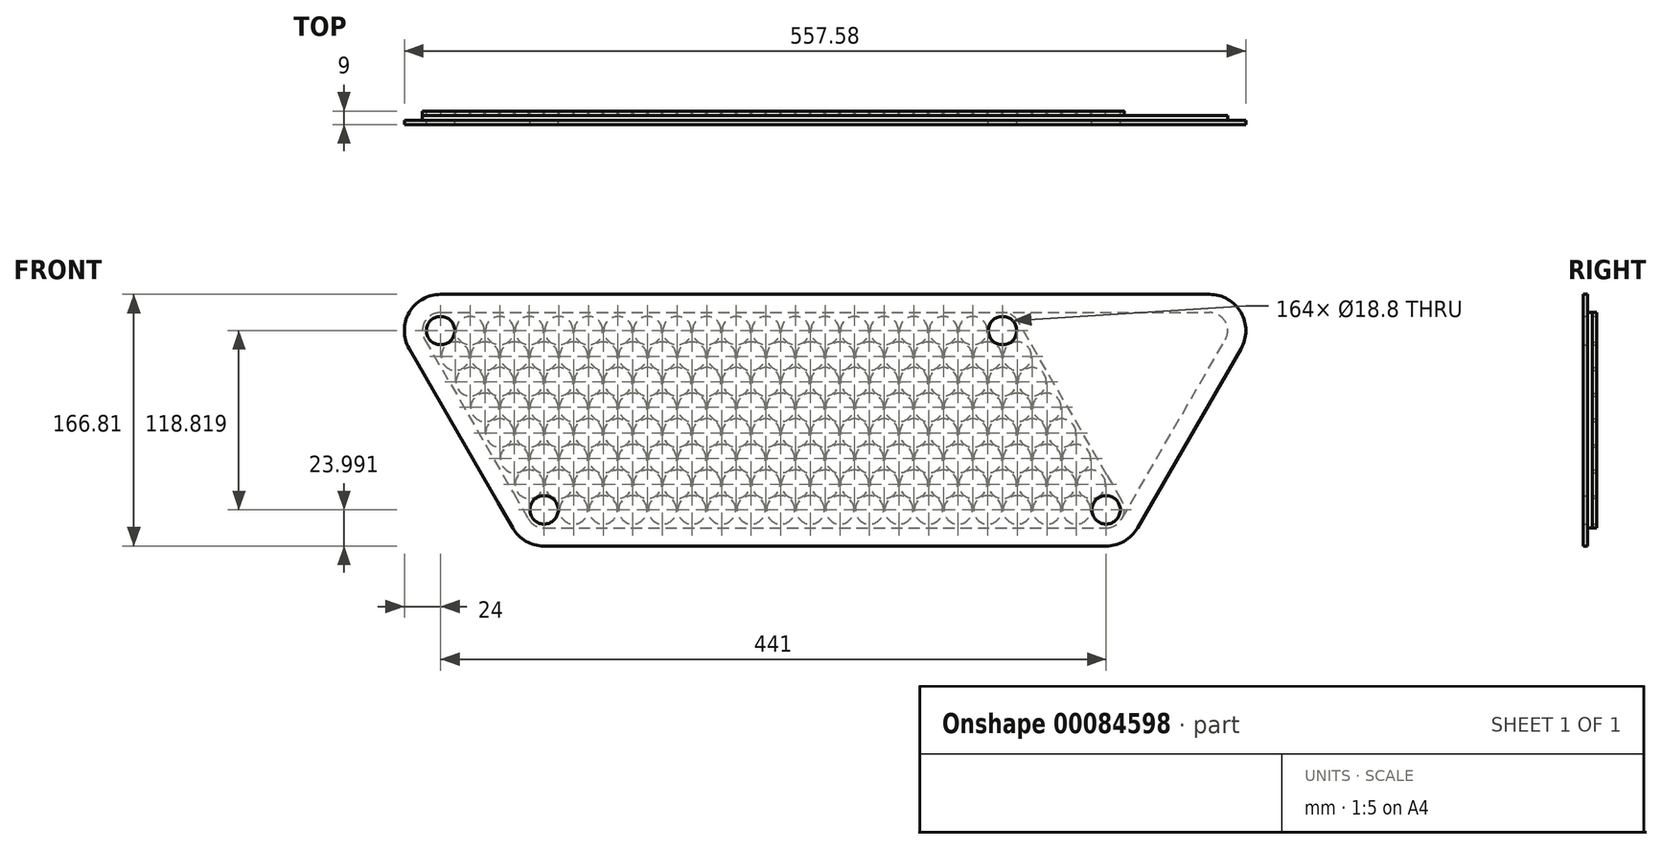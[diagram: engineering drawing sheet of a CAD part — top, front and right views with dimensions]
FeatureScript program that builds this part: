
annotation { "Feature Type Name" : "Feature", "Feature Type Description" : "" }
export const myFeature = defineFeature(function(context is Context, id is Id, definition is map)
    precondition{}
    {
        {
            var Q0;
            Q0=qCreatedBy(makeId("Front.planeOp"),FACE);
            var sketch = newSketch(context, id + "F0", { "sketchPlane" : qUnion([Q0]) });
            skLineSegment(sketch, "E0", {"start": v(0, 0) * mm, "end": v(79.44, 0) * mm, "construction": true});
            skLineSegment(sketch, "E1", {"start": v(0, 0) * mm, "end": v(43.4, -75.16) * mm, "construction": true});
            skCircle(sketch, "E2", {"center": v(0, 0) * mm, "radius": 9.4 * mm});
            skCircle(sketch, "E3.1.0.0", {"center": v(19.6, 0) * mm, "radius": 9.4 * mm});
            skCircle(sketch, "E3.2.0.0", {"center": v(39.2, 0) * mm, "radius": 9.4 * mm});
            skCircle(sketch, "E3.3.0.0", {"center": v(58.8, 0) * mm, "radius": 9.4 * mm});
            skCircle(sketch, "E3.4.0.0", {"center": v(78.4, 0) * mm, "radius": 9.4 * mm});
            skCircle(sketch, "E3.5.0.0", {"center": v(98, 0) * mm, "radius": 9.4 * mm});
            skCircle(sketch, "E3.6.0.0", {"center": v(117.6, 0) * mm, "radius": 9.4 * mm});
            skCircle(sketch, "E3.7.0.0", {"center": v(137.2, 0) * mm, "radius": 9.4 * mm});
            skCircle(sketch, "E3.8.0.0", {"center": v(156.8, 0) * mm, "radius": 9.4 * mm});
            skCircle(sketch, "E3.9.0.0", {"center": v(176.4, 0) * mm, "radius": 9.4 * mm});
            skCircle(sketch, "E3.10.0.0", {"center": v(196, 0) * mm, "radius": 9.4 * mm});
            skCircle(sketch, "E3.11.0.0", {"center": v(215.6, 0) * mm, "radius": 9.4 * mm});
            skCircle(sketch, "E3.12.0.0", {"center": v(235.2, 0) * mm, "radius": 9.4 * mm});
            skCircle(sketch, "E3.13.0.0", {"center": v(254.8, 0) * mm, "radius": 9.4 * mm});
            skCircle(sketch, "E3.14.0.0", {"center": v(274.4, 0) * mm, "radius": 9.4 * mm});
            skCircle(sketch, "E3.15.0.0", {"center": v(294, 0) * mm, "radius": 9.4 * mm});
            skCircle(sketch, "E3.16.0.0", {"center": v(313.6, 0) * mm, "radius": 9.4 * mm});
            skCircle(sketch, "E3.17.0.0", {"center": v(333.2, 0) * mm, "radius": 9.4 * mm});
            skCircle(sketch, "E3.18.0.0", {"center": v(352.8, 0) * mm, "radius": 9.4 * mm});
            skCircle(sketch, "E3.19.0.0", {"center": v(372.4, 0) * mm, "radius": 9.4 * mm});
            skLineSegment(sketch, "E3.direction1", {"start": v(0, 0) * mm, "end": v(19.6, 0) * mm, "construction": true});
            skCircle(sketch, "E4.1.0.0", {"center": v(9.8, -16.97) * mm, "radius": 9.4 * mm});
            skCircle(sketch, "E4.2.0.0", {"center": v(19.6, -33.95) * mm, "radius": 9.4 * mm});
            skCircle(sketch, "E4.3.0.0", {"center": v(29.4, -50.92) * mm, "radius": 9.4 * mm});
            skCircle(sketch, "E4.4.0.0", {"center": v(39.2, -67.9) * mm, "radius": 9.4 * mm});
            skCircle(sketch, "E4.5.0.0", {"center": v(49, -84.87) * mm, "radius": 9.4 * mm});
            skCircle(sketch, "E4.6.0.0", {"center": v(58.8, -101.84) * mm, "radius": 9.4 * mm});
            skLineSegment(sketch, "E4.direction1", {"start": v(0, 0) * mm, "end": v(9.8, -16.97) * mm, "construction": true});
            skCircle(sketch, "E5.1.0.0", {"center": v(29.4, -16.97) * mm, "radius": 9.4 * mm});
            skCircle(sketch, "E5.1.0.1", {"center": v(39.2, -33.95) * mm, "radius": 9.4 * mm});
            skCircle(sketch, "E5.1.0.2", {"center": v(49, -50.92) * mm, "radius": 9.4 * mm});
            skCircle(sketch, "E5.1.0.3", {"center": v(58.8, -67.9) * mm, "radius": 9.4 * mm});
            skCircle(sketch, "E5.1.0.4", {"center": v(68.6, -84.87) * mm, "radius": 9.4 * mm});
            skCircle(sketch, "E5.1.0.5", {"center": v(78.4, -101.84) * mm, "radius": 9.4 * mm});
            skCircle(sketch, "E5.2.0.0", {"center": v(49, -16.97) * mm, "radius": 9.4 * mm});
            skCircle(sketch, "E5.2.0.1", {"center": v(58.8, -33.95) * mm, "radius": 9.4 * mm});
            skCircle(sketch, "E5.2.0.2", {"center": v(68.6, -50.92) * mm, "radius": 9.4 * mm});
            skCircle(sketch, "E5.2.0.3", {"center": v(78.4, -67.9) * mm, "radius": 9.4 * mm});
            skCircle(sketch, "E5.2.0.4", {"center": v(88.2, -84.87) * mm, "radius": 9.4 * mm});
            skCircle(sketch, "E5.2.0.5", {"center": v(98, -101.84) * mm, "radius": 9.4 * mm});
            skCircle(sketch, "E5.3.0.0", {"center": v(68.6, -16.97) * mm, "radius": 9.4 * mm});
            skCircle(sketch, "E5.3.0.1", {"center": v(78.4, -33.95) * mm, "radius": 9.4 * mm});
            skCircle(sketch, "E5.3.0.2", {"center": v(88.2, -50.92) * mm, "radius": 9.4 * mm});
            skCircle(sketch, "E5.3.0.3", {"center": v(98, -67.9) * mm, "radius": 9.4 * mm});
            skCircle(sketch, "E5.3.0.4", {"center": v(107.8, -84.87) * mm, "radius": 9.4 * mm});
            skCircle(sketch, "E5.3.0.5", {"center": v(117.6, -101.84) * mm, "radius": 9.4 * mm});
            skCircle(sketch, "E5.4.0.0", {"center": v(88.2, -16.97) * mm, "radius": 9.4 * mm});
            skCircle(sketch, "E5.4.0.1", {"center": v(98, -33.95) * mm, "radius": 9.4 * mm});
            skCircle(sketch, "E5.4.0.2", {"center": v(107.8, -50.92) * mm, "radius": 9.4 * mm});
            skCircle(sketch, "E5.4.0.3", {"center": v(117.6, -67.9) * mm, "radius": 9.4 * mm});
            skCircle(sketch, "E5.4.0.4", {"center": v(127.4, -84.87) * mm, "radius": 9.4 * mm});
            skCircle(sketch, "E5.4.0.5", {"center": v(137.2, -101.84) * mm, "radius": 9.4 * mm});
            skCircle(sketch, "E5.5.0.0", {"center": v(107.8, -16.97) * mm, "radius": 9.4 * mm});
            skCircle(sketch, "E5.5.0.1", {"center": v(117.6, -33.95) * mm, "radius": 9.4 * mm});
            skCircle(sketch, "E5.5.0.2", {"center": v(127.4, -50.92) * mm, "radius": 9.4 * mm});
            skCircle(sketch, "E5.5.0.3", {"center": v(137.2, -67.9) * mm, "radius": 9.4 * mm});
            skCircle(sketch, "E5.5.0.4", {"center": v(147, -84.87) * mm, "radius": 9.4 * mm});
            skCircle(sketch, "E5.5.0.5", {"center": v(156.8, -101.84) * mm, "radius": 9.4 * mm});
            skCircle(sketch, "E5.6.0.0", {"center": v(127.4, -16.97) * mm, "radius": 9.4 * mm});
            skCircle(sketch, "E5.6.0.1", {"center": v(137.2, -33.95) * mm, "radius": 9.4 * mm});
            skCircle(sketch, "E5.6.0.2", {"center": v(147, -50.92) * mm, "radius": 9.4 * mm});
            skCircle(sketch, "E5.6.0.3", {"center": v(156.8, -67.9) * mm, "radius": 9.4 * mm});
            skCircle(sketch, "E5.6.0.4", {"center": v(166.6, -84.87) * mm, "radius": 9.4 * mm});
            skCircle(sketch, "E5.6.0.5", {"center": v(176.4, -101.84) * mm, "radius": 9.4 * mm});
            skCircle(sketch, "E5.7.0.0", {"center": v(147, -16.97) * mm, "radius": 9.4 * mm});
            skCircle(sketch, "E5.7.0.1", {"center": v(156.8, -33.95) * mm, "radius": 9.4 * mm});
            skCircle(sketch, "E5.7.0.2", {"center": v(166.6, -50.92) * mm, "radius": 9.4 * mm});
            skCircle(sketch, "E5.7.0.3", {"center": v(176.4, -67.9) * mm, "radius": 9.4 * mm});
            skCircle(sketch, "E5.7.0.4", {"center": v(186.2, -84.87) * mm, "radius": 9.4 * mm});
            skCircle(sketch, "E5.7.0.5", {"center": v(196, -101.84) * mm, "radius": 9.4 * mm});
            skCircle(sketch, "E5.8.0.0", {"center": v(166.6, -16.97) * mm, "radius": 9.4 * mm});
            skCircle(sketch, "E5.8.0.1", {"center": v(176.4, -33.95) * mm, "radius": 9.4 * mm});
            skCircle(sketch, "E5.8.0.2", {"center": v(186.2, -50.92) * mm, "radius": 9.4 * mm});
            skCircle(sketch, "E5.8.0.3", {"center": v(196, -67.9) * mm, "radius": 9.4 * mm});
            skCircle(sketch, "E5.8.0.4", {"center": v(205.8, -84.87) * mm, "radius": 9.4 * mm});
            skCircle(sketch, "E5.8.0.5", {"center": v(215.6, -101.84) * mm, "radius": 9.4 * mm});
            skCircle(sketch, "E5.9.0.0", {"center": v(186.2, -16.97) * mm, "radius": 9.4 * mm});
            skCircle(sketch, "E5.9.0.1", {"center": v(196, -33.95) * mm, "radius": 9.4 * mm});
            skCircle(sketch, "E5.9.0.2", {"center": v(205.8, -50.92) * mm, "radius": 9.4 * mm});
            skCircle(sketch, "E5.9.0.3", {"center": v(215.6, -67.9) * mm, "radius": 9.4 * mm});
            skCircle(sketch, "E5.9.0.4", {"center": v(225.4, -84.87) * mm, "radius": 9.4 * mm});
            skCircle(sketch, "E5.9.0.5", {"center": v(235.2, -101.84) * mm, "radius": 9.4 * mm});
            skCircle(sketch, "E5.10.0.0", {"center": v(205.8, -16.97) * mm, "radius": 9.4 * mm});
            skCircle(sketch, "E5.10.0.1", {"center": v(215.6, -33.95) * mm, "radius": 9.4 * mm});
            skCircle(sketch, "E5.10.0.2", {"center": v(225.4, -50.92) * mm, "radius": 9.4 * mm});
            skCircle(sketch, "E5.10.0.3", {"center": v(235.2, -67.9) * mm, "radius": 9.4 * mm});
            skCircle(sketch, "E5.10.0.4", {"center": v(245, -84.87) * mm, "radius": 9.4 * mm});
            skCircle(sketch, "E5.10.0.5", {"center": v(254.8, -101.84) * mm, "radius": 9.4 * mm});
            skCircle(sketch, "E5.11.0.0", {"center": v(225.4, -16.97) * mm, "radius": 9.4 * mm});
            skCircle(sketch, "E5.11.0.1", {"center": v(235.2, -33.95) * mm, "radius": 9.4 * mm});
            skCircle(sketch, "E5.11.0.2", {"center": v(245, -50.92) * mm, "radius": 9.4 * mm});
            skCircle(sketch, "E5.11.0.3", {"center": v(254.8, -67.9) * mm, "radius": 9.4 * mm});
            skCircle(sketch, "E5.11.0.4", {"center": v(264.6, -84.87) * mm, "radius": 9.4 * mm});
            skCircle(sketch, "E5.11.0.5", {"center": v(274.4, -101.84) * mm, "radius": 9.4 * mm});
            skCircle(sketch, "E5.12.0.0", {"center": v(245, -16.97) * mm, "radius": 9.4 * mm});
            skCircle(sketch, "E5.12.0.1", {"center": v(254.8, -33.95) * mm, "radius": 9.4 * mm});
            skCircle(sketch, "E5.12.0.2", {"center": v(264.6, -50.92) * mm, "radius": 9.4 * mm});
            skCircle(sketch, "E5.12.0.3", {"center": v(274.4, -67.9) * mm, "radius": 9.4 * mm});
            skCircle(sketch, "E5.12.0.4", {"center": v(284.2, -84.87) * mm, "radius": 9.4 * mm});
            skCircle(sketch, "E5.12.0.5", {"center": v(294, -101.84) * mm, "radius": 9.4 * mm});
            skCircle(sketch, "E5.13.0.0", {"center": v(264.6, -16.97) * mm, "radius": 9.4 * mm});
            skCircle(sketch, "E5.13.0.1", {"center": v(274.4, -33.95) * mm, "radius": 9.4 * mm});
            skCircle(sketch, "E5.13.0.2", {"center": v(284.2, -50.92) * mm, "radius": 9.4 * mm});
            skCircle(sketch, "E5.13.0.3", {"center": v(294, -67.9) * mm, "radius": 9.4 * mm});
            skCircle(sketch, "E5.13.0.4", {"center": v(303.8, -84.87) * mm, "radius": 9.4 * mm});
            skCircle(sketch, "E5.13.0.5", {"center": v(313.6, -101.84) * mm, "radius": 9.4 * mm});
            skCircle(sketch, "E5.14.0.0", {"center": v(284.2, -16.97) * mm, "radius": 9.4 * mm});
            skCircle(sketch, "E5.14.0.1", {"center": v(294, -33.95) * mm, "radius": 9.4 * mm});
            skCircle(sketch, "E5.14.0.2", {"center": v(303.8, -50.92) * mm, "radius": 9.4 * mm});
            skCircle(sketch, "E5.14.0.3", {"center": v(313.6, -67.9) * mm, "radius": 9.4 * mm});
            skCircle(sketch, "E5.14.0.4", {"center": v(323.4, -84.87) * mm, "radius": 9.4 * mm});
            skCircle(sketch, "E5.14.0.5", {"center": v(333.2, -101.84) * mm, "radius": 9.4 * mm});
            skCircle(sketch, "E5.15.0.0", {"center": v(303.8, -16.97) * mm, "radius": 9.4 * mm});
            skCircle(sketch, "E5.15.0.1", {"center": v(313.6, -33.95) * mm, "radius": 9.4 * mm});
            skCircle(sketch, "E5.15.0.2", {"center": v(323.4, -50.92) * mm, "radius": 9.4 * mm});
            skCircle(sketch, "E5.15.0.3", {"center": v(333.2, -67.9) * mm, "radius": 9.4 * mm});
            skCircle(sketch, "E5.15.0.4", {"center": v(343, -84.87) * mm, "radius": 9.4 * mm});
            skCircle(sketch, "E5.15.0.5", {"center": v(352.8, -101.84) * mm, "radius": 9.4 * mm});
            skCircle(sketch, "E5.16.0.0", {"center": v(323.4, -16.97) * mm, "radius": 9.4 * mm});
            skCircle(sketch, "E5.16.0.1", {"center": v(333.2, -33.95) * mm, "radius": 9.4 * mm});
            skCircle(sketch, "E5.16.0.2", {"center": v(343, -50.92) * mm, "radius": 9.4 * mm});
            skCircle(sketch, "E5.16.0.3", {"center": v(352.8, -67.9) * mm, "radius": 9.4 * mm});
            skCircle(sketch, "E5.16.0.4", {"center": v(362.6, -84.87) * mm, "radius": 9.4 * mm});
            skCircle(sketch, "E5.16.0.5", {"center": v(372.4, -101.84) * mm, "radius": 9.4 * mm});
            skCircle(sketch, "E5.17.0.0", {"center": v(343, -16.97) * mm, "radius": 9.4 * mm});
            skCircle(sketch, "E5.17.0.1", {"center": v(352.8, -33.95) * mm, "radius": 9.4 * mm});
            skCircle(sketch, "E5.17.0.2", {"center": v(362.6, -50.92) * mm, "radius": 9.4 * mm});
            skCircle(sketch, "E5.17.0.3", {"center": v(372.4, -67.9) * mm, "radius": 9.4 * mm});
            skCircle(sketch, "E5.17.0.4", {"center": v(382.2, -84.87) * mm, "radius": 9.4 * mm});
            skCircle(sketch, "E5.17.0.5", {"center": v(392, -101.84) * mm, "radius": 9.4 * mm});
            skCircle(sketch, "E5.18.0.0", {"center": v(362.6, -16.97) * mm, "radius": 9.4 * mm});
            skCircle(sketch, "E5.18.0.1", {"center": v(372.4, -33.95) * mm, "radius": 9.4 * mm});
            skCircle(sketch, "E5.18.0.2", {"center": v(382.2, -50.92) * mm, "radius": 9.4 * mm});
            skCircle(sketch, "E5.18.0.3", {"center": v(392, -67.9) * mm, "radius": 9.4 * mm});
            skCircle(sketch, "E5.18.0.4", {"center": v(401.8, -84.87) * mm, "radius": 9.4 * mm});
            skCircle(sketch, "E5.18.0.5", {"center": v(411.6, -101.84) * mm, "radius": 9.4 * mm});
            skCircle(sketch, "E5.19.0.0", {"center": v(382.2, -16.97) * mm, "radius": 9.4 * mm});
            skCircle(sketch, "E5.19.0.1", {"center": v(392, -33.95) * mm, "radius": 9.4 * mm});
            skCircle(sketch, "E5.19.0.2", {"center": v(401.8, -50.92) * mm, "radius": 9.4 * mm});
            skCircle(sketch, "E5.19.0.3", {"center": v(411.6, -67.9) * mm, "radius": 9.4 * mm});
            skCircle(sketch, "E5.19.0.4", {"center": v(421.4, -84.87) * mm, "radius": 9.4 * mm});
            skCircle(sketch, "E5.19.0.5", {"center": v(431.2, -101.84) * mm, "radius": 9.4 * mm});
            skLineSegment(sketch, "E5.direction1", {"start": v(9.8, -16.97) * mm, "end": v(29.4, -16.97) * mm, "construction": true});
            skLineSegment(sketch, "E6", {"start": v(0, 0) * mm, "end": v(372.4, 0) * mm, "construction": true});
            skLineSegment(sketch, "E7", {"start": v(372.4, 0) * mm, "end": v(441, -118.8) * mm, "construction": true});
            skLineSegment(sketch, "E8", {"start": v(441, -118.8) * mm, "end": v(68.6, -118.8) * mm, "construction": true});
            skLineSegment(sketch, "E9", {"start": v(68.6, -118.8) * mm, "end": v(0, 0) * mm, "construction": true});
            skArc(sketch, "E10", {"start": v(382.8, 6) * mm, "mid": v(378.4, 10.4) * mm, "end": v(372.4, 12) * mm});
            skArc(sketch, "E11", {"start": v(0, 12) * mm, "mid": v(-10.4, 6) * mm, "end": v(-10.4, -6) * mm});
            skLineSegment(sketch, "E12", {"start": v(0, 12) * mm, "end": v(372.4, 12) * mm});
            skLineSegment(sketch, "E13", {"start": v(-10.4, -6) * mm, "end": v(48.4, -107.84) * mm});
            skLineSegment(sketch, "E14", {"start": v(441.6, -95.84) * mm, "end": v(382.8, 6) * mm});
            skCircle(sketch, "E15.0.7.0", {"center": v(68.6, -118.82) * mm, "radius": 9.4 * mm});
            skCircle(sketch, "E16.1.0.0", {"center": v(88.2, -118.82) * mm, "radius": 9.4 * mm});
            skCircle(sketch, "E16.2.0.0", {"center": v(107.8, -118.82) * mm, "radius": 9.4 * mm});
            skCircle(sketch, "E16.3.0.0", {"center": v(127.4, -118.82) * mm, "radius": 9.4 * mm});
            skCircle(sketch, "E16.4.0.0", {"center": v(147, -118.82) * mm, "radius": 9.4 * mm});
            skCircle(sketch, "E16.5.0.0", {"center": v(166.6, -118.82) * mm, "radius": 9.4 * mm});
            skCircle(sketch, "E16.6.0.0", {"center": v(186.2, -118.82) * mm, "radius": 9.4 * mm});
            skCircle(sketch, "E16.7.0.0", {"center": v(205.8, -118.82) * mm, "radius": 9.4 * mm});
            skCircle(sketch, "E16.8.0.0", {"center": v(225.4, -118.82) * mm, "radius": 9.4 * mm});
            skCircle(sketch, "E16.9.0.0", {"center": v(245, -118.82) * mm, "radius": 9.4 * mm});
            skCircle(sketch, "E16.10.0.0", {"center": v(264.6, -118.82) * mm, "radius": 9.4 * mm});
            skCircle(sketch, "E16.11.0.0", {"center": v(284.2, -118.82) * mm, "radius": 9.4 * mm});
            skCircle(sketch, "E16.12.0.0", {"center": v(303.8, -118.82) * mm, "radius": 9.4 * mm});
            skCircle(sketch, "E16.13.0.0", {"center": v(323.4, -118.82) * mm, "radius": 9.4 * mm});
            skCircle(sketch, "E16.14.0.0", {"center": v(343, -118.82) * mm, "radius": 9.4 * mm});
            skCircle(sketch, "E16.15.0.0", {"center": v(362.6, -118.82) * mm, "radius": 9.4 * mm});
            skCircle(sketch, "E16.16.0.0", {"center": v(382.2, -118.82) * mm, "radius": 9.4 * mm});
            skCircle(sketch, "E16.17.0.0", {"center": v(401.8, -118.82) * mm, "radius": 9.4 * mm});
            skCircle(sketch, "E16.18.0.0", {"center": v(421.4, -118.82) * mm, "radius": 9.4 * mm});
            skCircle(sketch, "E16.19.0.0", {"center": v(441, -118.82) * mm, "radius": 9.4 * mm});
            skLineSegment(sketch, "E16.direction1", {"start": v(68.6, -118.82) * mm, "end": v(88.2, -118.82) * mm, "construction": true});
            skArc(sketch, "E17", {"start": v(58.2, -124.8) * mm, "mid": v(62.6, -129.2) * mm, "end": v(68.6, -130.8) * mm});
            skLineSegment(sketch, "E18", {"start": v(48.4, -107.84) * mm, "end": v(58.2, -124.8) * mm});
            skLineSegment(sketch, "E19", {"start": v(441.6, -95.84) * mm, "end": v(451.38, -112.8) * mm});
            skArc(sketch, "E20.trimOffspring", {"start": v(441, -130.8) * mm, "mid": v(451.38, -124.8) * mm, "end": v(451.38, -112.8) * mm});
            skLineSegment(sketch, "E21", {"start": v(68.6, -130.8) * mm, "end": v(441, -130.8) * mm});
            skArc(sketch, "E22.trimOffspring", {"start": v(80.6, -118.82) * mm, "mid": v(80.6, -118.81) * mm, "end": v(80.6, -118.8) * mm});
            skLineSegment(sketch, "E23", {"start": v(441, -130.8) * mm, "end": v(587.8, -130.8) * mm, "construction": true});
            skLineSegment(sketch, "E24", {"start": v(451.38, -124.8) * mm, "end": v(519.98, -6) * mm, "construction": true});
            skLineSegment(sketch, "E25", {"start": v(372.4, 12) * mm, "end": v(509.58, 12) * mm, "construction": true});
            skArc(sketch, "E26.filletArc", {"start": v(519.98, -6) * mm, "mid": v(519.98, 6) * mm, "end": v(509.58, 12) * mm, "construction": true});
            skSolve(sketch);
        }
        {
            var Q0;
            Q0=makeQuery(id+"F0.imprint","IMPRINT",FACE,{"disambiguationData":[TD([[makeQuery(id+"F0.imprint","IMPRINT",EDGE,{"derivedFrom":sQuery(id+"F0.wireOp",EDGE,"E2")}),-1.0]])]});
            extrude(context, id + "F1", {"entities" : qUnion([Q0]), "depth" : 3 * mm});
        }
        {
            var Q0;
            Q0=makeQuery(id+"F1.opExtrude","CAP_FACE",FACE,{"disambiguationData":[OSD([sQuery(id+"F0.wireOp",EDGE,"E2"),sQuery(id+"F0.wireOp",EDGE,"E3.1.0.0"),sQuery(id+"F0.wireOp",EDGE,"E3.2.0.0"),sQuery(id+"F0.wireOp",EDGE,"E3.3.0.0"),sQuery(id+"F0.wireOp",EDGE,"E3.4.0.0"),sQuery(id+"F0.wireOp",EDGE,"E3.5.0.0"),sQuery(id+"F0.wireOp",EDGE,"E3.6.0.0"),sQuery(id+"F0.wireOp",EDGE,"E3.7.0.0"),sQuery(id+"F0.wireOp",EDGE,"E3.8.0.0"),sQuery(id+"F0.wireOp",EDGE,"E3.9.0.0"),sQuery(id+"F0.wireOp",EDGE,"E3.10.0.0"),sQuery(id+"F0.wireOp",EDGE,"E3.11.0.0"),sQuery(id+"F0.wireOp",EDGE,"E3.12.0.0"),sQuery(id+"F0.wireOp",EDGE,"E3.13.0.0"),sQuery(id+"F0.wireOp",EDGE,"E3.14.0.0"),sQuery(id+"F0.wireOp",EDGE,"E3.15.0.0"),sQuery(id+"F0.wireOp",EDGE,"E3.16.0.0"),sQuery(id+"F0.wireOp",EDGE,"E3.17.0.0"),sQuery(id+"F0.wireOp",EDGE,"E3.18.0.0"),sQuery(id+"F0.wireOp",EDGE,"E3.19.0.0"),sQuery(id+"F0.wireOp",EDGE,"E4.1.0.0"),sQuery(id+"F0.wireOp",EDGE,"E4.2.0.0"),sQuery(id+"F0.wireOp",EDGE,"E4.3.0.0"),sQuery(id+"F0.wireOp",EDGE,"E4.4.0.0"),sQuery(id+"F0.wireOp",EDGE,"E4.5.0.0"),sQuery(id+"F0.wireOp",EDGE,"E4.6.0.0"),sQuery(id+"F0.wireOp",EDGE,"E5.1.0.0"),sQuery(id+"F0.wireOp",EDGE,"E5.1.0.1"),sQuery(id+"F0.wireOp",EDGE,"E5.1.0.2"),sQuery(id+"F0.wireOp",EDGE,"E5.1.0.3"),sQuery(id+"F0.wireOp",EDGE,"E5.1.0.4"),sQuery(id+"F0.wireOp",EDGE,"E5.1.0.5"),sQuery(id+"F0.wireOp",EDGE,"E5.2.0.0"),sQuery(id+"F0.wireOp",EDGE,"E5.2.0.1"),sQuery(id+"F0.wireOp",EDGE,"E5.2.0.2"),sQuery(id+"F0.wireOp",EDGE,"E5.2.0.3"),sQuery(id+"F0.wireOp",EDGE,"E5.2.0.4"),sQuery(id+"F0.wireOp",EDGE,"E5.2.0.5"),sQuery(id+"F0.wireOp",EDGE,"E5.3.0.0"),sQuery(id+"F0.wireOp",EDGE,"E5.3.0.1"),sQuery(id+"F0.wireOp",EDGE,"E5.3.0.2"),sQuery(id+"F0.wireOp",EDGE,"E5.3.0.3"),sQuery(id+"F0.wireOp",EDGE,"E5.3.0.4"),sQuery(id+"F0.wireOp",EDGE,"E5.3.0.5"),sQuery(id+"F0.wireOp",EDGE,"E5.4.0.0"),sQuery(id+"F0.wireOp",EDGE,"E5.4.0.1"),sQuery(id+"F0.wireOp",EDGE,"E5.4.0.2"),sQuery(id+"F0.wireOp",EDGE,"E5.4.0.3"),sQuery(id+"F0.wireOp",EDGE,"E5.4.0.4"),sQuery(id+"F0.wireOp",EDGE,"E5.4.0.5"),sQuery(id+"F0.wireOp",EDGE,"E5.5.0.0"),sQuery(id+"F0.wireOp",EDGE,"E5.5.0.1"),sQuery(id+"F0.wireOp",EDGE,"E5.5.0.2"),sQuery(id+"F0.wireOp",EDGE,"E5.5.0.3"),sQuery(id+"F0.wireOp",EDGE,"E5.5.0.4"),sQuery(id+"F0.wireOp",EDGE,"E5.5.0.5"),sQuery(id+"F0.wireOp",EDGE,"E5.6.0.0"),sQuery(id+"F0.wireOp",EDGE,"E5.6.0.1"),sQuery(id+"F0.wireOp",EDGE,"E5.6.0.2"),sQuery(id+"F0.wireOp",EDGE,"E5.6.0.3"),sQuery(id+"F0.wireOp",EDGE,"E5.6.0.4"),sQuery(id+"F0.wireOp",EDGE,"E5.6.0.5"),sQuery(id+"F0.wireOp",EDGE,"E5.7.0.0"),sQuery(id+"F0.wireOp",EDGE,"E5.7.0.1"),sQuery(id+"F0.wireOp",EDGE,"E5.7.0.2"),sQuery(id+"F0.wireOp",EDGE,"E5.7.0.3"),sQuery(id+"F0.wireOp",EDGE,"E5.7.0.4"),sQuery(id+"F0.wireOp",EDGE,"E5.7.0.5"),sQuery(id+"F0.wireOp",EDGE,"E5.8.0.0"),sQuery(id+"F0.wireOp",EDGE,"E5.8.0.1"),sQuery(id+"F0.wireOp",EDGE,"E5.8.0.2"),sQuery(id+"F0.wireOp",EDGE,"E5.8.0.3"),sQuery(id+"F0.wireOp",EDGE,"E5.8.0.4"),sQuery(id+"F0.wireOp",EDGE,"E5.8.0.5"),sQuery(id+"F0.wireOp",EDGE,"E5.9.0.0"),sQuery(id+"F0.wireOp",EDGE,"E5.9.0.1"),sQuery(id+"F0.wireOp",EDGE,"E5.9.0.2"),sQuery(id+"F0.wireOp",EDGE,"E5.9.0.3"),sQuery(id+"F0.wireOp",EDGE,"E5.9.0.4"),sQuery(id+"F0.wireOp",EDGE,"E5.9.0.5"),sQuery(id+"F0.wireOp",EDGE,"E5.10.0.0"),sQuery(id+"F0.wireOp",EDGE,"E5.10.0.1"),sQuery(id+"F0.wireOp",EDGE,"E5.10.0.2"),sQuery(id+"F0.wireOp",EDGE,"E5.10.0.3"),sQuery(id+"F0.wireOp",EDGE,"E5.10.0.4"),sQuery(id+"F0.wireOp",EDGE,"E5.10.0.5"),sQuery(id+"F0.wireOp",EDGE,"E5.11.0.0"),sQuery(id+"F0.wireOp",EDGE,"E5.11.0.1"),sQuery(id+"F0.wireOp",EDGE,"E5.11.0.2"),sQuery(id+"F0.wireOp",EDGE,"E5.11.0.3"),sQuery(id+"F0.wireOp",EDGE,"E5.11.0.4"),sQuery(id+"F0.wireOp",EDGE,"E5.11.0.5"),sQuery(id+"F0.wireOp",EDGE,"E5.12.0.0"),sQuery(id+"F0.wireOp",EDGE,"E5.12.0.1"),sQuery(id+"F0.wireOp",EDGE,"E5.12.0.2"),sQuery(id+"F0.wireOp",EDGE,"E5.12.0.3"),sQuery(id+"F0.wireOp",EDGE,"E5.12.0.4"),sQuery(id+"F0.wireOp",EDGE,"E5.12.0.5"),sQuery(id+"F0.wireOp",EDGE,"E5.13.0.0"),sQuery(id+"F0.wireOp",EDGE,"E5.13.0.1"),sQuery(id+"F0.wireOp",EDGE,"E5.13.0.2"),sQuery(id+"F0.wireOp",EDGE,"E5.13.0.3"),sQuery(id+"F0.wireOp",EDGE,"E5.13.0.4"),sQuery(id+"F0.wireOp",EDGE,"E5.13.0.5"),sQuery(id+"F0.wireOp",EDGE,"E5.14.0.0"),sQuery(id+"F0.wireOp",EDGE,"E5.14.0.1"),sQuery(id+"F0.wireOp",EDGE,"E5.14.0.2"),sQuery(id+"F0.wireOp",EDGE,"E5.14.0.3"),sQuery(id+"F0.wireOp",EDGE,"E5.14.0.4"),sQuery(id+"F0.wireOp",EDGE,"E5.14.0.5"),sQuery(id+"F0.wireOp",EDGE,"E5.15.0.0"),sQuery(id+"F0.wireOp",EDGE,"E5.15.0.1"),sQuery(id+"F0.wireOp",EDGE,"E5.15.0.2"),sQuery(id+"F0.wireOp",EDGE,"E5.15.0.3"),sQuery(id+"F0.wireOp",EDGE,"E5.15.0.4"),sQuery(id+"F0.wireOp",EDGE,"E5.15.0.5"),sQuery(id+"F0.wireOp",EDGE,"E5.16.0.0"),sQuery(id+"F0.wireOp",EDGE,"E5.16.0.1"),sQuery(id+"F0.wireOp",EDGE,"E5.16.0.2"),sQuery(id+"F0.wireOp",EDGE,"E5.16.0.3"),sQuery(id+"F0.wireOp",EDGE,"E5.16.0.4"),sQuery(id+"F0.wireOp",EDGE,"E5.16.0.5"),sQuery(id+"F0.wireOp",EDGE,"E5.17.0.0"),sQuery(id+"F0.wireOp",EDGE,"E5.17.0.1"),sQuery(id+"F0.wireOp",EDGE,"E5.17.0.2"),sQuery(id+"F0.wireOp",EDGE,"E5.17.0.3"),sQuery(id+"F0.wireOp",EDGE,"E5.17.0.4"),sQuery(id+"F0.wireOp",EDGE,"E5.17.0.5"),sQuery(id+"F0.wireOp",EDGE,"E5.18.0.0"),sQuery(id+"F0.wireOp",EDGE,"E5.18.0.1"),sQuery(id+"F0.wireOp",EDGE,"E5.18.0.2"),sQuery(id+"F0.wireOp",EDGE,"E5.18.0.3"),sQuery(id+"F0.wireOp",EDGE,"E5.18.0.4"),sQuery(id+"F0.wireOp",EDGE,"E5.18.0.5"),sQuery(id+"F0.wireOp",EDGE,"E5.19.0.0"),sQuery(id+"F0.wireOp",EDGE,"E5.19.0.1"),sQuery(id+"F0.wireOp",EDGE,"E5.19.0.2"),sQuery(id+"F0.wireOp",EDGE,"E5.19.0.3"),sQuery(id+"F0.wireOp",EDGE,"E5.19.0.4"),sQuery(id+"F0.wireOp",EDGE,"E5.19.0.5"),sQuery(id+"F0.wireOp",EDGE,"E10"),sQuery(id+"F0.wireOp",EDGE,"E11"),sQuery(id+"F0.wireOp",EDGE,"E12"),sQuery(id+"F0.wireOp",EDGE,"E13"),sQuery(id+"F0.wireOp",EDGE,"E14"),sQuery(id+"F0.wireOp",EDGE,"E15.0.7.0"),sQuery(id+"F0.wireOp",EDGE,"E16.1.0.0"),sQuery(id+"F0.wireOp",EDGE,"E16.2.0.0"),sQuery(id+"F0.wireOp",EDGE,"E16.3.0.0"),sQuery(id+"F0.wireOp",EDGE,"E16.4.0.0"),sQuery(id+"F0.wireOp",EDGE,"E16.5.0.0"),sQuery(id+"F0.wireOp",EDGE,"E16.6.0.0"),sQuery(id+"F0.wireOp",EDGE,"E16.7.0.0"),sQuery(id+"F0.wireOp",EDGE,"E16.8.0.0"),sQuery(id+"F0.wireOp",EDGE,"E16.9.0.0"),sQuery(id+"F0.wireOp",EDGE,"E16.10.0.0"),sQuery(id+"F0.wireOp",EDGE,"E16.11.0.0"),sQuery(id+"F0.wireOp",EDGE,"E16.12.0.0"),sQuery(id+"F0.wireOp",EDGE,"E16.13.0.0"),sQuery(id+"F0.wireOp",EDGE,"E16.14.0.0"),sQuery(id+"F0.wireOp",EDGE,"E16.15.0.0"),sQuery(id+"F0.wireOp",EDGE,"E16.16.0.0"),sQuery(id+"F0.wireOp",EDGE,"E16.17.0.0"),sQuery(id+"F0.wireOp",EDGE,"E16.18.0.0"),sQuery(id+"F0.wireOp",EDGE,"E16.19.0.0"),sQuery(id+"F0.wireOp",EDGE,"E17"),sQuery(id+"F0.wireOp",EDGE,"E18"),sQuery(id+"F0.wireOp",EDGE,"E19"),sQuery(id+"F0.wireOp",EDGE,"E20.trimOffspring"),sQuery(id+"F0.wireOp",EDGE,"E21")])],"isStart":false});
            var sketch = newSketch(context, id + "F2", { "sketchPlane" : qUnion([Q0]) });
            skLineSegment(sketch, "E27.0", {"start": v(0, 12) * mm, "end": v(372.4, 12) * mm});
            skArc(sketch, "E27.1", {"start": v(0, 12) * mm, "mid": v(-10.4, 6) * mm, "end": v(-10.4, -6) * mm});
            skLineSegment(sketch, "E27.2", {"start": v(-10.4, -6) * mm, "end": v(48.4, -107.84) * mm});
            skLineSegment(sketch, "E27.3", {"start": v(48.4, -107.84) * mm, "end": v(58.2, -124.8) * mm});
            skArc(sketch, "E27.4", {"start": v(58.2, -124.8) * mm, "mid": v(62.6, -129.2) * mm, "end": v(68.6, -130.8) * mm});
            skLineSegment(sketch, "E27.5", {"start": v(68.6, -130.8) * mm, "end": v(441, -130.8) * mm});
            skArc(sketch, "E27.6", {"start": v(441, -130.8) * mm, "mid": v(447, -129.2) * mm, "end": v(451.38, -124.8) * mm});
            skLineSegment(sketch, "E28.0", {"start": v(372.4, 12) * mm, "end": v(509.58, 12) * mm});
            skArc(sketch, "E28.1", {"start": v(519.98, -6) * mm, "mid": v(519.98, 6) * mm, "end": v(509.58, 12) * mm});
            skLineSegment(sketch, "E28.2", {"start": v(451.38, -124.8) * mm, "end": v(519.98, -6) * mm});
            skPoint(sketch, "E27.7.end.orphan", {"position": v(382.8, 6) * mm});
            skPoint(sketch, "E27.8.end.orphan", {"position": v(451.38, -112.8) * mm});
            skPoint(sketch, "E27.8.start.orphan", {"position": v(441.6, -95.84) * mm});
            skSolve(sketch);
        }
        {
            var Q0;
            Q0 = qSketchRegion(id + "F2", true);
            extrude(context, id + "F3", {"entities" : qUnion([Q0]), "depth" : 3 * mm});
        }
        {
            var Q0;
            Q0=makeQuery(id+"F3.opExtrude","CAP_FACE",FACE,{"disambiguationData":[OSD([sQuery(id+"F2.wireOp",EDGE,"E27.0"),sQuery(id+"F2.wireOp",EDGE,"E27.1"),sQuery(id+"F2.wireOp",EDGE,"E27.2"),sQuery(id+"F2.wireOp",EDGE,"E27.3"),sQuery(id+"F2.wireOp",EDGE,"E27.4"),sQuery(id+"F2.wireOp",EDGE,"E27.5"),sQuery(id+"F2.wireOp",EDGE,"E27.6"),sQuery(id+"F2.wireOp",EDGE,"E28.0"),sQuery(id+"F2.wireOp",EDGE,"E28.1"),sQuery(id+"F2.wireOp",EDGE,"E28.2")])],"isStart":false});
            var sketch = newSketch(context, id + "F4", { "sketchPlane" : qUnion([Q0]) });
            skLineSegment(sketch, "E29.0", {"start": v(0, 12) * mm, "end": v(509.58, 12) * mm, "construction": true});
            skArc(sketch, "E29.1", {"start": v(519.98, -6) * mm, "mid": v(519.98, 6) * mm, "end": v(509.58, 12) * mm, "construction": true});
            skLineSegment(sketch, "E29.2", {"start": v(451.38, -124.8) * mm, "end": v(519.98, -6) * mm, "construction": true});
            skArc(sketch, "E29.3", {"start": v(441, -130.8) * mm, "mid": v(447, -129.2) * mm, "end": v(451.38, -124.8) * mm, "construction": true});
            skLineSegment(sketch, "E29.4", {"start": v(68.6, -130.8) * mm, "end": v(441, -130.8) * mm, "construction": true});
            skArc(sketch, "E29.5", {"start": v(58.2, -124.8) * mm, "mid": v(62.6, -129.2) * mm, "end": v(68.6, -130.8) * mm, "construction": true});
            skLineSegment(sketch, "E29.6", {"start": v(48.4, -107.84) * mm, "end": v(58.2, -124.8) * mm, "construction": true});
            skLineSegment(sketch, "E29.7", {"start": v(-10.4, -6) * mm, "end": v(48.4, -107.84) * mm, "construction": true});
            skArc(sketch, "E29.8", {"start": v(0, 12) * mm, "mid": v(-10.4, 6) * mm, "end": v(-10.4, -6) * mm, "construction": true});
            skArc(sketch, "E30.0", {"start": v(0, 24) * mm, "mid": v(-20.78, 12) * mm, "end": v(-20.78, -12) * mm});
            skLineSegment(sketch, "E30.1", {"start": v(0, 24) * mm, "end": v(509.58, 24) * mm});
            skLineSegment(sketch, "E30.2", {"start": v(-20.78, -12) * mm, "end": v(38.02, -113.84) * mm});
            skArc(sketch, "E30.3", {"start": v(530.37, -12) * mm, "mid": v(530.37, 12) * mm, "end": v(509.58, 24) * mm});
            skLineSegment(sketch, "E30.4", {"start": v(461.78, -130.8) * mm, "end": v(530.37, -12) * mm});
            skLineSegment(sketch, "E30.5", {"start": v(38.02, -113.84) * mm, "end": v(47.8, -130.8) * mm});
            skArc(sketch, "E30.6", {"start": v(47.8, -130.8) * mm, "mid": v(56.6, -139.6) * mm, "end": v(68.6, -142.8) * mm});
            skLineSegment(sketch, "E30.7", {"start": v(68.6, -142.8) * mm, "end": v(441, -142.8) * mm});
            skArc(sketch, "E30.8", {"start": v(441, -142.8) * mm, "mid": v(453, -139.6) * mm, "end": v(461.78, -130.8) * mm});
            skCircle(sketch, "E31.0", {"center": v(0, 0) * mm, "radius": 9.4 * mm});
            skCircle(sketch, "E31.1", {"center": v(68.6, -118.82) * mm, "radius": 9.4 * mm});
            skCircle(sketch, "E31.2", {"center": v(372.4, 0) * mm, "radius": 9.4 * mm});
            skCircle(sketch, "E31.3", {"center": v(441, -118.82) * mm, "radius": 9.4 * mm});
            skSolve(sketch);
        }
        {
            var Q0;
            Q0=makeQuery(id+"F4.imprint","IMPRINT",FACE,{"disambiguationData":[TD([[makeQuery(id+"F4.imprint","IMPRINT",EDGE,{"derivedFrom":sQuery(id+"F4.wireOp",EDGE,"E30.0")}),1.0]])]});
            var Q1;
            Q1=makeQuery(id+"F4.imprint","IMPRINT",FACE,{"disambiguationData":[TD([[makeQuery(id+"F4.imprint","IMPRINT",EDGE,{"derivedFrom":makeQuery(id+"F3.opExtrude","CAP_EDGE",EDGE,{"disambiguationData":[OSD([sQuery(id+"F2.wireOp",EDGE,"E27.1")])],"isStart":false})}),1.0]])]});
            extrude(context, id + "F5", {"entities" : qUnion([Q0, Q1]), "depth" : 3 * mm});
        }
    });
